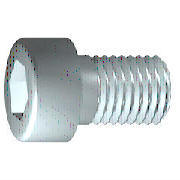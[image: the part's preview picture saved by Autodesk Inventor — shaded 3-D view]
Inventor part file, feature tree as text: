
AUTODESK INVENTOR PART (.ipt)
format: ipt  version: 2024 (Build 280153000, 153)  size: 186,368 bytes
history: native  units: mm (DEFAULTED — no unit token found)
features: fillet x2, sketch x2, extrude x1, thread x1, chamfer x1, plane x1
ambient origin geometry x7: Origin, YZ Plane, XY Plane, X Axis, Y Axis, Z Axis, Center Point
bodies: Solid1 (feature_tree), Body (feature_tree)
feature tree (8):
  extrude  "Slot"  Depth=3.0mm
  fillet  "Fillet1"  Radius=3.0mm
  thread  "Thread"  [1 undecoded]
  chamfer  "Chamfer1"  Distance=3.0mm
  plane  "Work Plane1"
  fillet  "Fillet2"  Radius=3.0mm
  sketch  "Sketch1"  dims[d1=18.75mm d2=0.306825mm d3=3.0mm d4=1.3mm]
  sketch  "Sketch2"  dims[d5=60.0deg d6=3.0mm d7=3.0mm d8=2.886751mm d9=5.5mm d10=90.0deg d11=10.0mm d12=0.0mm d13=18.75mm d14=0.0mm d15=0.306725mm d16=0.306725mm d17=0.3mm d19=0.0mm d26=20.0mm d27=45.0deg d28=0.0mm d29=0.0mm d30=0.1mm]
note: 1 required parameter value undecoded (feature->parameter linkage not recoverable at this tier; creation-order binding heuristic only, values carry confidence <= 0.55)
